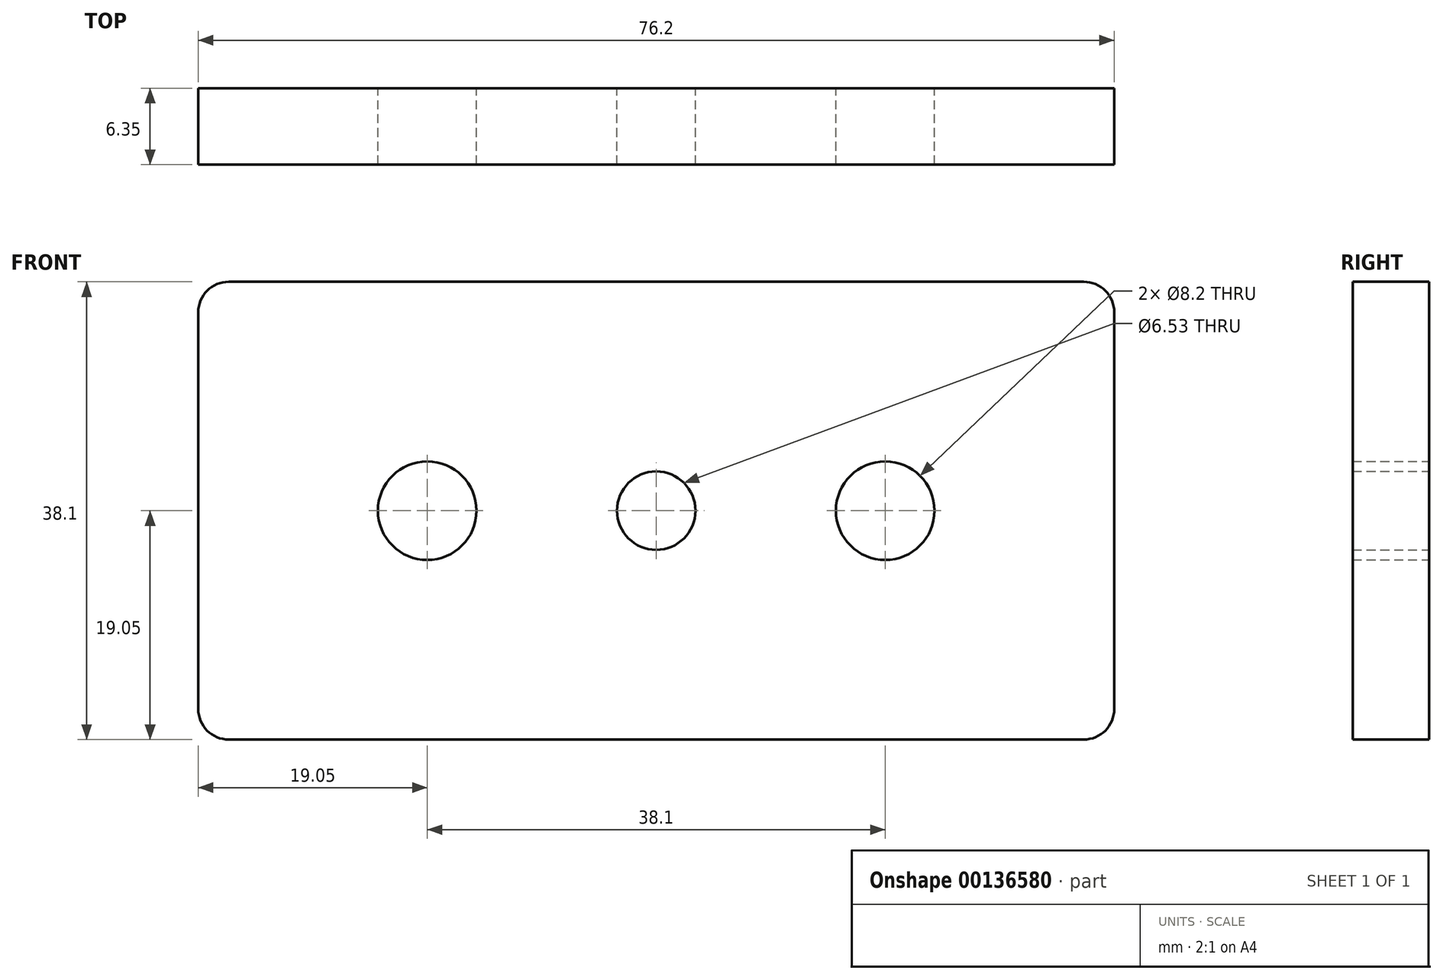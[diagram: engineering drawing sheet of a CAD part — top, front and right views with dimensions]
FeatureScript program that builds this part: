
annotation { "Feature Type Name" : "Feature", "Feature Type Description" : "" }
export const myFeature = defineFeature(function(context is Context, id is Id, definition is map)
    precondition{}
    {
        {
            var Q0;
            Q0=qCreatedBy(makeId("Front.planeOp"),FACE);
            var sketch = newSketch(context, id + "F0", { "sketchPlane" : qUnion([Q0])});
            skLineSegment(sketch, "E0.bottom", {"start": v(2.54, 0) * mm, "end": v(73.66, 0) * mm});
            skLineSegment(sketch, "E0.top", {"start": v(2.54, 38.1) * mm, "end": v(73.66, 38.1) * mm});
            skLineSegment(sketch, "E0.left", {"start": v(0, 2.54) * mm, "end": v(0, 35.56) * mm});
            skLineSegment(sketch, "E0.right", {"start": v(76.2, 2.54) * mm, "end": v(76.2, 35.56) * mm});
            skPoint(sketch, "E1.visualSharp", {"position": v(0, 38.1) * mm});
            skArc(sketch, "E1.filletArc", {"start": v(2.54, 38.1) * mm, "mid": v(0.74, 37.36) * mm, "end": v(0, 35.56) * mm});
            skPoint(sketch, "E2.visualSharp", {"position": v(76.2, 38.1) * mm});
            skArc(sketch, "E2.filletArc", {"start": v(76.2, 35.56) * mm, "mid": v(75.46, 37.36) * mm, "end": v(73.66, 38.1) * mm});
            skPoint(sketch, "E3.visualSharp", {"position": v(76.2, 0) * mm});
            skArc(sketch, "E3.filletArc", {"start": v(73.66, 0) * mm, "mid": v(75.46, 0.74) * mm, "end": v(76.2, 2.54) * mm});
            skPoint(sketch, "E4.visualSharp", {"position": v(0, 0) * mm});
            skArc(sketch, "E4.filletArc", {"start": v(0, 2.54) * mm, "mid": v(0.74, 0.74) * mm, "end": v(2.54, 0) * mm});
            skLineSegment(sketch, "E5", {"start": v(0, 19.05) * mm, "end": v(76.2, 19.05) * mm, "construction": true});
            skCircle(sketch, "E6", {"center": v(19.05, 19.05) * mm, "radius": 4.1 * mm});
            skCircle(sketch, "E7", {"center": v(38.1, 19.05) * mm, "radius": 3.26 * mm});
            skCircle(sketch, "E8", {"center": v(57.15, 19.05) * mm, "radius": 4.1 * mm});
            skSolve(sketch);
        }
        {
            var Q0;
            Q0=makeQuery(id+"F0.imprint","IMPRINT",FACE,{"disambiguationData":[TD([[makeQuery(id+"F0.imprint","IMPRINT",EDGE,{"derivedFrom":sQuery(id+"F0.wireOp",EDGE,"E0.bottom")}),1.0]])]});
            extrude(context, id + "F1", {"entities" : qUnion([Q0]), "depth" : 6.35 * mm});
        }
    });
